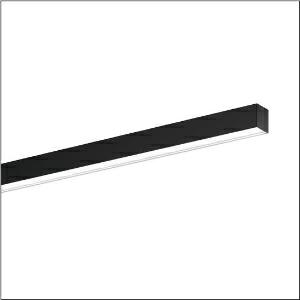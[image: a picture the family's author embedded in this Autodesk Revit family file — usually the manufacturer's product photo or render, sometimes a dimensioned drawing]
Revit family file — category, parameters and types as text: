
# Revit family: silica_r__21_51mx23da34bb_8ce5
name_source: partatom
category: Lighting Fixtures
units: mm (PartAtom-declared; Revit-internal decimal feet)

## family parameters
Cut with Voids When Loaded = No
Host = Face
Light Source = No
Part Type = Normal
Room Calculation Point = No
Round Connector Dimension = Use Diameter
Shared = No

## types (1)
- --- (1 x LED, 3280 lm, 24.1 W, 3000K)
    Apparent Load = 24 VA
    CIE Flux Codes = 78 96 99 100 100
    Color Rendering = 80
    Color Temperature = 3000K
    Default Elevation = 1800 mm
    Description = Silica® 21, office luminaire, primary optical cover: prismatic diffuser, of PMMA, CAT 2 (L<= 3000cd/m²), light emission: direct distribution, primary light characteristic: symmetric, installation type: surface-mounted, LED, rated luminous flux: 3.280lm, luminous efficacy: 136lm/W, light colour: 830, colour temperature: 3000K, with terminal, 3+2-pole, max. 2.5mm², mains connection: 220..240V, AC, 50/60Hz, rated input power: 24.1W, luminaire housing, of aluminium, jet black (RAL 9005), length: 1.204mm, width: 53mm, height: 53mm, protection rating (complete): IP20, insulation class (complete): insulation class I (protective earthing), certification: CE, permissible operating ambient temperature: 0..+35°C, standard: EN 50419, packaging unit: 1 piece
    Height = 0 mm  [stored 0 ft]
    Lamp = 1 x LED
    Lamp Light Flux = 3280 lm
    Lamp Power = 24.1 W
    Lamp count = 1
    Length = 1204 mm
    Luminous efficacy = 136 lm/W
    Manufacturer = Siteco
    ModVariant = No
    Model = 51MX23DA34BB
    Mounting Place = Ceiling
    Mounting Type = Recessed
    Number of Poles = 1
    OnlyDefault = Yes
    Power Factor = 1
    Product Name = Silica® 21
    Product group = office luminaire | ceiling recessed
    ProductGroupID = 401
    Protection Class = Protection class I
    Protection Degree = IP 20
    RLX_Detail_Level = 1
    RLX_Emergency_Light_Flux = 0 lm
    RLX_Emergency_Type = 0
    RLX_Emergency_Type_DB = No
    RlxData = <blob elided: 23761 chars, md5=2b618883>
    Socket = socket
    Standby Power = 0 W
    System Light Flux = 3280 lm
    System Power = 24 W
    Type Comments = factory setting: luminous flux: 100 % | dim-lin: 254 | 345 mA
    Type Image = l_1313584.jpg
    URL = http://relux.com
    VarID = @adj_068149
    Voltage = 0 V
    Weight = 0.00 kg
    Width = 53 mm

note: [stored X ft] marks values corroborated as IEEE doubles in the binary element streams (Revit-internal decimal feet)

## geometry (parser evidence)
native form markers: Blend x4, Sweep x12
no freeform markers — native parametric forms only
